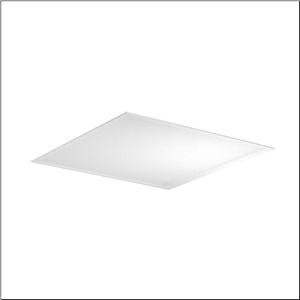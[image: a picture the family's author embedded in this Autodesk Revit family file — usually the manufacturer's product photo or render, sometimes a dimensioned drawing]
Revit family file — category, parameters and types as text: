
# Revit family: apollon_r__21_square_51mq12wd2454_4918
name_source: partatom
category: Lighting Fixtures
units: mm (PartAtom-declared; Revit-internal decimal feet)

## family parameters
Cut with Voids When Loaded = No
Host = Face
Light Source = No
Part Type = Normal
Room Calculation Point = No
Round Connector Dimension = Use Diameter
Shared = No

## types (1)
- Apollon® 21 square (1 x LED, 4200 lm, 24.7 W, 4000K)
    Apparent Load = 25 VA
    CIE Flux Codes = 60 87 97 100 100
    Color Rendering = 80
    Color Temperature = 4000K
    Default Elevation = 1800 mm
    Description = Apollon® 21 square, office luminaire, primary optical cover: micro prismatic cover, of PMMA, CAT 2 (L<= 3000cd/m²), light emission: direct distribution, primary light characteristic: symmetric, installation type: lay-in mounting, LED, rated luminous flux: 4.200lm, luminous efficacy: 170lm/W, light colour: 840, colour temperature: 4000K, with terminal, 5-pole, mains connection: 220..240V, AC/DC, 0/50..60Hz, rated input power: 24.7W, housing, of aluminium, coated, traffic white (RAL 9016), module: M600, length: 595mm, width: 595mm, height: 30mm, housing upper side, of sheet steel, galvanised, protection rating (complete): IP20, protection rating (lamp compartment, on room side): IP54, insulation class (complete): insulation class II (safety insulation), certification: CE, ENEC, impact resistance: IK03, permissible operating ambient temperature: -20..+45°C, permissible storage temperature: -40..+80°C, packaging unit: 1 piece
    Height = 0 mm  [stored 0 ft]
    Lamp = 1 x LED
    Lamp Light Flux = 4200 lm
    Lamp Power = 24.7 W
    Lamp count = 1
    Length = 595 mm
    Luminous efficacy = 170 lm/W
    Manufacturer = Siteco
    ModVariant = No
    Model = 51MQ12WD2454
    Mounting Place = Ceiling
    Mounting Type = Recessed
    Number of Poles = 1
    OnlyDefault = Yes
    Power Factor = 1
    Product Name = Apollon® 21 square
    Product group = office luminaire | ceiling recessed
    ProductGroupID = 401
    Protection Class = Protection class II
    Protection Degree = IP 20
    RLX_Detail_Level = 1
    RLX_Emergency_Light_Flux = 0 lm
    RLX_Emergency_Type = 0
    RLX_Emergency_Type_DB = No
    RlxData = <blob elided: 12501 chars, md5=ec586058>
    Socket = socket
    Standby Power = 0 W
    System Light Flux = 4200 lm
    System Power = 25 W
    Type Comments = Product without accessories
    Type Image = l_1291049.jpg
    URL = http://relux.com
    VarID = ---
    Voltage = 0 V
    Weight = 0.00 kg
    Width = 595 mm

note: [stored X ft] marks values corroborated as IEEE doubles in the binary element streams (Revit-internal decimal feet)

## geometry (parser evidence)
native form markers: Sweep x11
no freeform markers — native parametric forms only
